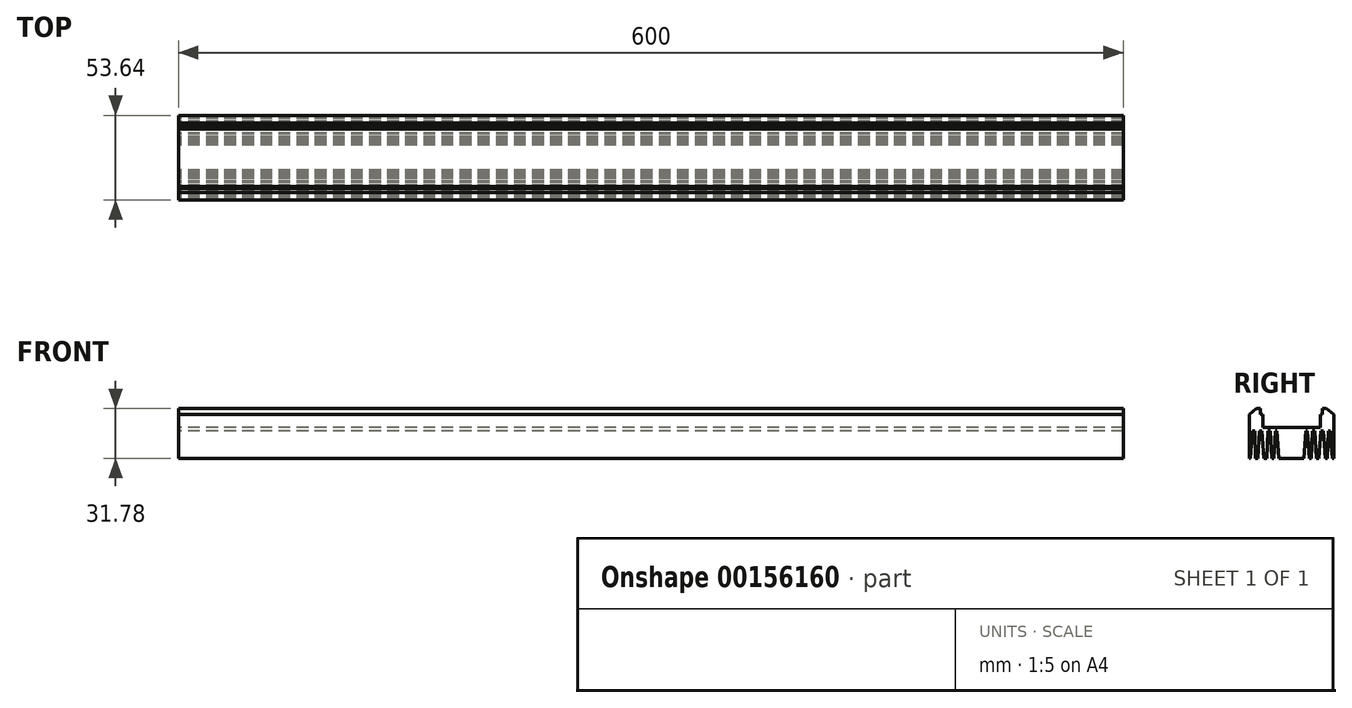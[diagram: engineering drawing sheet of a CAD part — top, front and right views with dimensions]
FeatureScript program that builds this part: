
annotation { "Feature Type Name" : "Feature", "Feature Type Description" : "" }
export const myFeature = defineFeature(function(context is Context, id is Id, definition is map)
    precondition{}
    {
        {
            var Q0;
            Q0=qCreatedBy(makeId("Right.planeOp"),FACE);
            var sketch = newSketch(context, id + "F0", { "sketchPlane" : qUnion([Q0])});
            skLineSegment(sketch, "E0.bottom", {"start": v(-22.12, 15.9) * mm, "end": v(-19.76, 15.9) * mm});
            skLineSegment(sketch, "E0.top", {"start": v(-26.82, -15.9) * mm, "end": v(-25.93, -15.9) * mm});
            skLineSegment(sketch, "E0.left", {"start": v(-26.82, 12.2) * mm, "end": v(-26.82, -15.9) * mm});
            skLineSegment(sketch, "E0.right", {"start": v(26.82, 12.2) * mm, "end": v(26.82, -15.9) * mm});
            skPoint(sketch, "E0.middle", {"position": v(0, 0) * mm});
            skLineSegment(sketch, "E1", {"start": v(-26.82, 12.2) * mm, "end": v(-22.12, 15.9) * mm});
            skLineSegment(sketch, "E2", {"start": v(-19.76, 15.9) * mm, "end": v(-19.76, 12.02) * mm});
            skLineSegment(sketch, "E3", {"start": v(-19.76, 12.02) * mm, "end": v(-18.25, 12.02) * mm});
            skLineSegment(sketch, "E4", {"start": v(-18.25, 12.02) * mm, "end": v(-18.25, 3.78) * mm});
            skLineSegment(sketch, "E5", {"start": v(-18.25, 3.78) * mm, "end": v(0, 3.78) * mm});
            skPoint(sketch, "E6.orphan", {"position": v(-26.82, 15.9) * mm});
            skLineSegment(sketch, "E7.MirrorCS", {"start": v(18.25, 3.78) * mm, "end": v(0, 3.78) * mm});
            skLineSegment(sketch, "E8.MirrorCS", {"start": v(18.25, 12.02) * mm, "end": v(18.25, 3.78) * mm});
            skLineSegment(sketch, "E9.MirrorCS", {"start": v(19.76, 12.02) * mm, "end": v(18.25, 12.02) * mm});
            skLineSegment(sketch, "E10.MirrorCS", {"start": v(19.76, 15.9) * mm, "end": v(19.76, 12.02) * mm});
            skLineSegment(sketch, "E11.MirrorCS", {"start": v(22.12, 15.9) * mm, "end": v(19.76, 15.9) * mm});
            skLineSegment(sketch, "E12.MirrorCS", {"start": v(26.82, 12.2) * mm, "end": v(22.12, 15.9) * mm});
            skPoint(sketch, "E13.orphan", {"position": v(26.82, 15.9) * mm});
            skLineSegment(sketch, "E14", {"start": v(-25.93, -15.9) * mm, "end": v(-24.83, 1.7) * mm});
            skLineSegment(sketch, "E15", {"start": v(-24.83, 1.7) * mm, "end": v(-23.33, 1.7) * mm});
            skLineSegment(sketch, "E16", {"start": v(-23.33, 1.7) * mm, "end": v(-22.93, -15.9) * mm});
            skLineSegment(sketch, "E17", {"start": v(-21.43, -15.9) * mm, "end": v(-20.33, 1.7) * mm});
            skLineSegment(sketch, "E18.trimOffspring", {"start": v(-22.93, -15.9) * mm, "end": v(-21.43, -15.9) * mm});
            skLineSegment(sketch, "E19.trimOffspring", {"start": v(-20.33, 1.7) * mm, "end": v(-18.83, 1.7) * mm});
            skLineSegment(sketch, "E20", {"start": v(-18.83, 1.7) * mm, "end": v(-17.53, -15.9) * mm});
            skLineSegment(sketch, "E21", {"start": v(-17.53, -15.9) * mm, "end": v(-15.75, -15.9) * mm});
            skLineSegment(sketch, "E22", {"start": v(-15.75, -15.9) * mm, "end": v(-14.86, 1.7) * mm});
            skLineSegment(sketch, "E23", {"start": v(-14.86, 1.7) * mm, "end": v(-13.32, 1.7) * mm});
            skLineSegment(sketch, "E24", {"start": v(-13.32, 1.7) * mm, "end": v(-12.55, -15.9) * mm});
            skLineSegment(sketch, "E25", {"start": v(-12.55, -15.9) * mm, "end": v(-11.3, -15.9) * mm});
            skLineSegment(sketch, "E26", {"start": v(-11.3, -15.9) * mm, "end": v(-10.16, 1.7) * mm});
            skLineSegment(sketch, "E27", {"start": v(-10.16, 1.7) * mm, "end": v(-9.23, 1.7) * mm});
            skLineSegment(sketch, "E28", {"start": v(-9.23, 1.7) * mm, "end": v(-7.98, -15.9) * mm});
            skLineSegment(sketch, "E29.trimOffspring", {"start": v(-7.98, -15.9) * mm, "end": v(7.98, -15.9) * mm});
            skPoint(sketch, "E30.orphan", {"position": v(0, 1.7) * mm});
            skLineSegment(sketch, "E31", {"start": v(0, 3.78) * mm, "end": v(0, -4.64) * mm, "construction": true});
            skLineSegment(sketch, "E32.MirrorCS", {"start": v(-4.7, -15.43) * mm, "end": v(-8.3, 1.83) * mm});
            skLineSegment(sketch, "E33.MirrorCS", {"start": v(9.23, 1.7) * mm, "end": v(7.98, -15.9) * mm});
            skLineSegment(sketch, "E34.MirrorCS", {"start": v(11.3, -15.9) * mm, "end": v(10.16, 1.7) * mm});
            skLineSegment(sketch, "E35.MirrorCS", {"start": v(13.32, 1.7) * mm, "end": v(12.55, -15.9) * mm});
            skLineSegment(sketch, "E36.MirrorCS", {"start": v(15.75, -15.9) * mm, "end": v(14.86, 1.7) * mm});
            skLineSegment(sketch, "E37.MirrorCS", {"start": v(18.83, 1.7) * mm, "end": v(17.53, -15.9) * mm});
            skLineSegment(sketch, "E38.MirrorCS", {"start": v(21.43, -15.9) * mm, "end": v(20.33, 1.7) * mm});
            skLineSegment(sketch, "E39.MirrorCS", {"start": v(23.33, 1.7) * mm, "end": v(22.93, -15.9) * mm});
            skLineSegment(sketch, "E40.MirrorCS", {"start": v(25.93, -15.9) * mm, "end": v(24.83, 1.7) * mm});
            skLineSegment(sketch, "E41.MirrorCS", {"start": v(20.33, 1.7) * mm, "end": v(18.83, 1.7) * mm});
            skLineSegment(sketch, "E42.MirrorCS", {"start": v(14.86, 1.7) * mm, "end": v(13.32, 1.7) * mm});
            skLineSegment(sketch, "E43.MirrorCS", {"start": v(10.16, 1.7) * mm, "end": v(9.23, 1.7) * mm});
            skLineSegment(sketch, "E44.MirrorCS", {"start": v(24.83, 1.7) * mm, "end": v(23.33, 1.7) * mm});
            skLineSegment(sketch, "E45.trimOffspring", {"start": v(25.93, -15.9) * mm, "end": v(26.82, -15.9) * mm});
            skLineSegment(sketch, "E46.trimOffspring", {"start": v(21.43, -15.9) * mm, "end": v(22.93, -15.9) * mm});
            skLineSegment(sketch, "E47.trimOffspring", {"start": v(15.75, -15.9) * mm, "end": v(17.53, -15.9) * mm});
            skLineSegment(sketch, "E48.trimOffspring", {"start": v(11.3, -15.9) * mm, "end": v(12.55, -15.9) * mm});
            skSolve(sketch);
        }
        {
            var Q0;
            Q0 = qSketchRegion(id + "F0", true);
            extrude(context, id + "F1", {"entities" : qUnion([Q0]), "depth" : 600 * mm});
        }
    });
